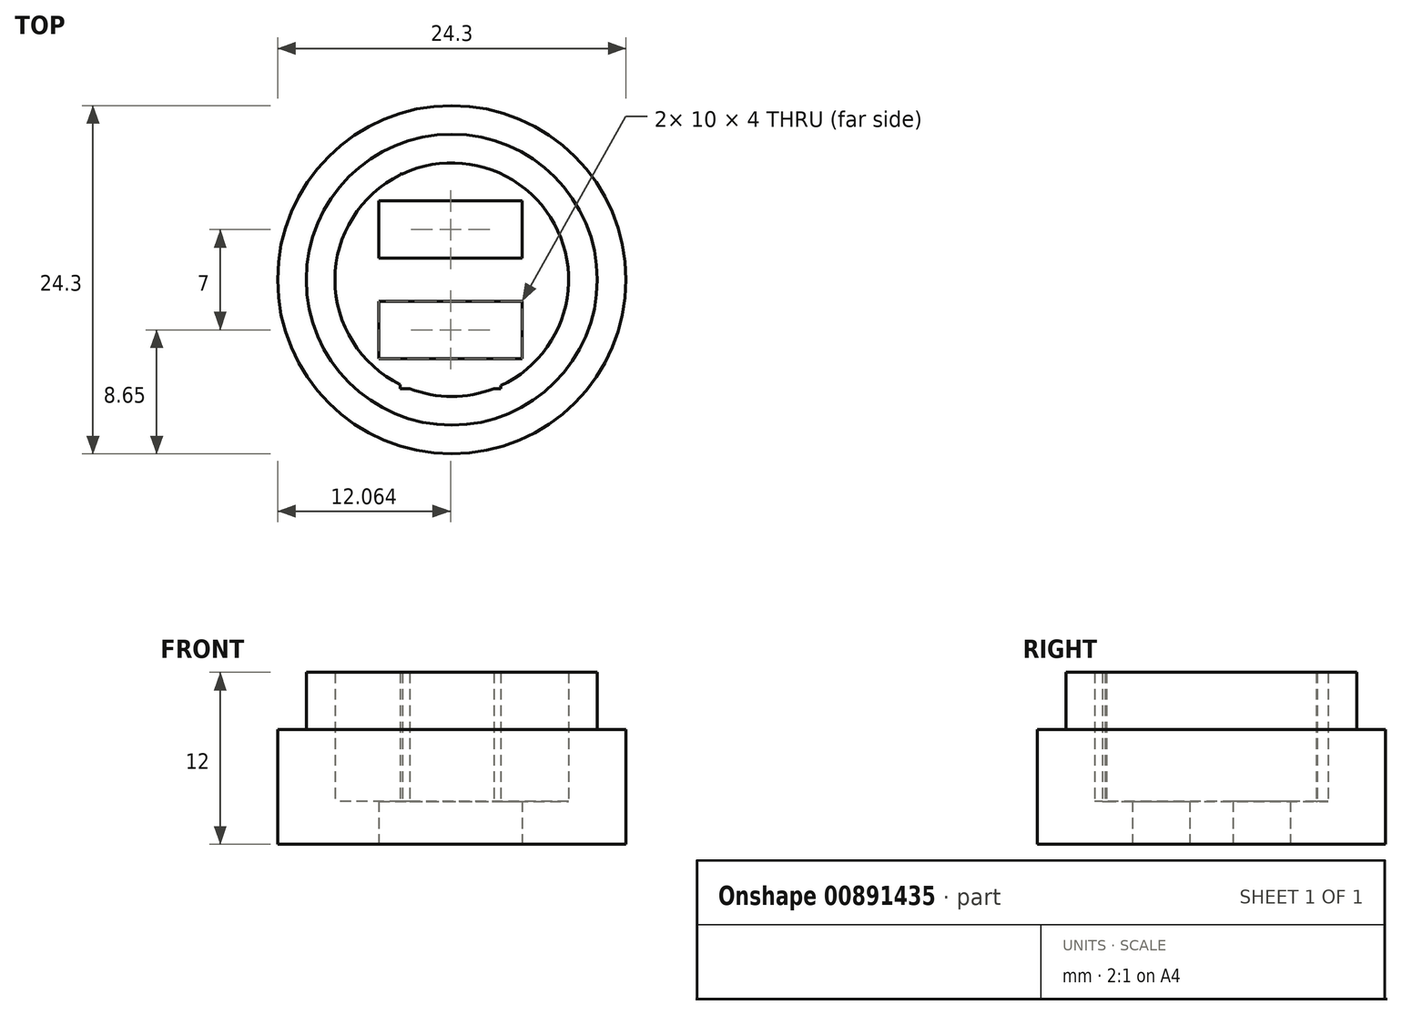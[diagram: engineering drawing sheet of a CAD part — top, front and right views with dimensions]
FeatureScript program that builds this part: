
annotation { "Feature Type Name" : "Feature", "Feature Type Description" : "" }
export const myFeature = defineFeature(function(context is Context, id is Id, definition is map)
    precondition{}
    {
        {
            var Q0;
            Q0=qCreatedBy(makeId("Top.planeOp"),FACE);
            var sketch = newSketch(context, id + "F0", { "sketchPlane" : qUnion([Q0])});
            skCircle(sketch, "E0", {"center": v(0, 0) * mm, "radius": 10.15 * mm});
            skCircle(sketch, "E1", {"center": v(0, 0) * mm, "radius": 8.15 * mm});
            skSolve(sketch);
        }
        {
            var Q0;
            Q0 = qSketchRegion(id + "F0", true);
            extrude(context, id + "F1", {"entities" : qUnion([Q0]), "depth" : 4 * mm, "offsetDistance" : 25.4 * mm});
        }
        {
            var Q0;
            Q0=makeQuery(id+"F1.opExtrude","CAP_FACE",FACE,{"disambiguationData":[OSD([sQuery(id+"F0.wireOp",EDGE,"E0"),sQuery(id+"F0.wireOp",EDGE,"E1")])],"isStart":true});
            var sketch = newSketch(context, id + "F2", { "sketchPlane" : qUnion([Q0])});
            skCircle(sketch, "E2", {"center": v(0, 0) * mm, "radius": 8.15 * mm});
            skCircle(sketch, "E3", {"center": v(0, 0) * mm, "radius": 12.15 * mm});
            skSolve(sketch);
        }
        {
            var Q0;
            Q0 = qSketchRegion(id + "F2", true);
            extrude(context, id + "F3", {"entities" : qUnion([Q0]), "operationType" : NewBodyOperationType.ADD, "depth" : 8 * mm, "offsetDistance" : 25.4 * mm});
        }
        {
            var Q0;
            Q0=makeQuery(id+"F3.opExtrude","CAP_FACE",FACE,{"disambiguationData":[OSD([sQuery(id+"F2.wireOp",EDGE,"E2"),sQuery(id+"F2.wireOp",EDGE,"E3")])],"isStart":false});
            var sketch = newSketch(context, id + "F4", { "sketchPlane" : qUnion([Q0])});
            skLineSegment(sketch, "E4.bottom", {"start": v(3.41, 7.6) * mm, "end": v(-3.59, 7.6) * mm});
            skLineSegment(sketch, "E4.top", {"start": v(3.41, -7.4) * mm, "end": v(-3.59, -7.4) * mm});
            skLineSegment(sketch, "E4.left", {"start": v(3.41, 7.6) * mm, "end": v(3.41, -7.4) * mm});
            skLineSegment(sketch, "E4.right", {"start": v(-3.59, 7.6) * mm, "end": v(-3.59, -7.4) * mm});
            skSolve(sketch);
        }
        {
            var Q0;
            Q0 = qSketchRegion(id + "F4", true);
            extrude(context, id + "F5", {"entities" : qUnion([Q0]), "operationType" : NewBodyOperationType.REMOVE, "oppositeDirection" : true, "depth" : 17.27 * mm, "offsetDistance" : 25.4 * mm});
        }
        {
            var Q0;
            Q0=makeQuery(id+"F3.opExtrude","CAP_FACE",FACE,{"disambiguationData":[OSD([sQuery(id+"F2.wireOp",EDGE,"E2"),sQuery(id+"F2.wireOp",EDGE,"E3")])],"isStart":false});
            var sketch = newSketch(context, id + "F6", { "sketchPlane" : qUnion([Q0])});
            skLineSegment(sketch, "E5.0", {"start": v(-3.59, -7.32) * mm, "end": v(-3.59, -7.4) * mm});
            skLineSegment(sketch, "E5.1", {"start": v(3.41, 7.6) * mm, "end": v(2.93, 7.6) * mm});
            skArc(sketch, "E5.2", {"start": v(-2.93, 7.6) * mm, "mid": v(0, 8.15) * mm, "end": v(2.93, 7.6) * mm});
            skLineSegment(sketch, "E5.3", {"start": v(-2.93, 7.6) * mm, "end": v(-3.59, 7.6) * mm});
            skLineSegment(sketch, "E5.4", {"start": v(-3.59, 7.6) * mm, "end": v(-3.59, 7.32) * mm});
            skLineSegment(sketch, "E5.5", {"start": v(3.41, 7.6) * mm, "end": v(3.41, 7.4) * mm});
            skArc(sketch, "E5.6", {"start": v(-3.59, -7.32) * mm, "mid": v(-8.15, 0) * mm, "end": v(-3.59, 7.32) * mm});
            skArc(sketch, "E5.7", {"start": v(3.41, 7.4) * mm, "mid": v(8.15, 0) * mm, "end": v(3.41, -7.4) * mm});
            skLineSegment(sketch, "E5.8", {"start": v(3.41, -7.4) * mm, "end": v(3.41, -7.4) * mm});
            skLineSegment(sketch, "E5.9", {"start": v(3.43, -7.4) * mm, "end": v(3.41, -7.4) * mm});
            skArc(sketch, "E5.10", {"start": v(3.43, -7.4) * mm, "mid": v(0, -8.15) * mm, "end": v(-3.43, -7.4) * mm});
            skLineSegment(sketch, "E5.11", {"start": v(-3.43, -7.4) * mm, "end": v(-3.59, -7.4) * mm});
            skLineSegment(sketch, "E6.bottom", {"start": v(-5.09, 5.5) * mm, "end": v(4.91, 5.5) * mm});
            skLineSegment(sketch, "E6.top", {"start": v(-5.09, 1.5) * mm, "end": v(4.91, 1.5) * mm});
            skLineSegment(sketch, "E6.left", {"start": v(-5.09, 5.5) * mm, "end": v(-5.09, 1.5) * mm});
            skLineSegment(sketch, "E6.right", {"start": v(4.91, 5.5) * mm, "end": v(4.91, 1.5) * mm});
            skLineSegment(sketch, "E7.bottom", {"start": v(-5.09, -5.5) * mm, "end": v(4.91, -5.5) * mm});
            skLineSegment(sketch, "E7.top", {"start": v(-5.09, -1.5) * mm, "end": v(4.91, -1.5) * mm});
            skLineSegment(sketch, "E7.left", {"start": v(-5.09, -5.5) * mm, "end": v(-5.09, -1.5) * mm});
            skLineSegment(sketch, "E7.right", {"start": v(4.91, -5.5) * mm, "end": v(4.91, -1.5) * mm});
            skSolve(sketch);
        }
        {
            var Q0;
            Q0 = qSketchRegion(id + "F6", true);
            extrude(context, id + "F7", {"entities" : qUnion([Q0]), "operationType" : NewBodyOperationType.ADD, "oppositeDirection" : true, "depth" : 3 * mm, "offsetDistance" : 25.4 * mm});
        }
    });
